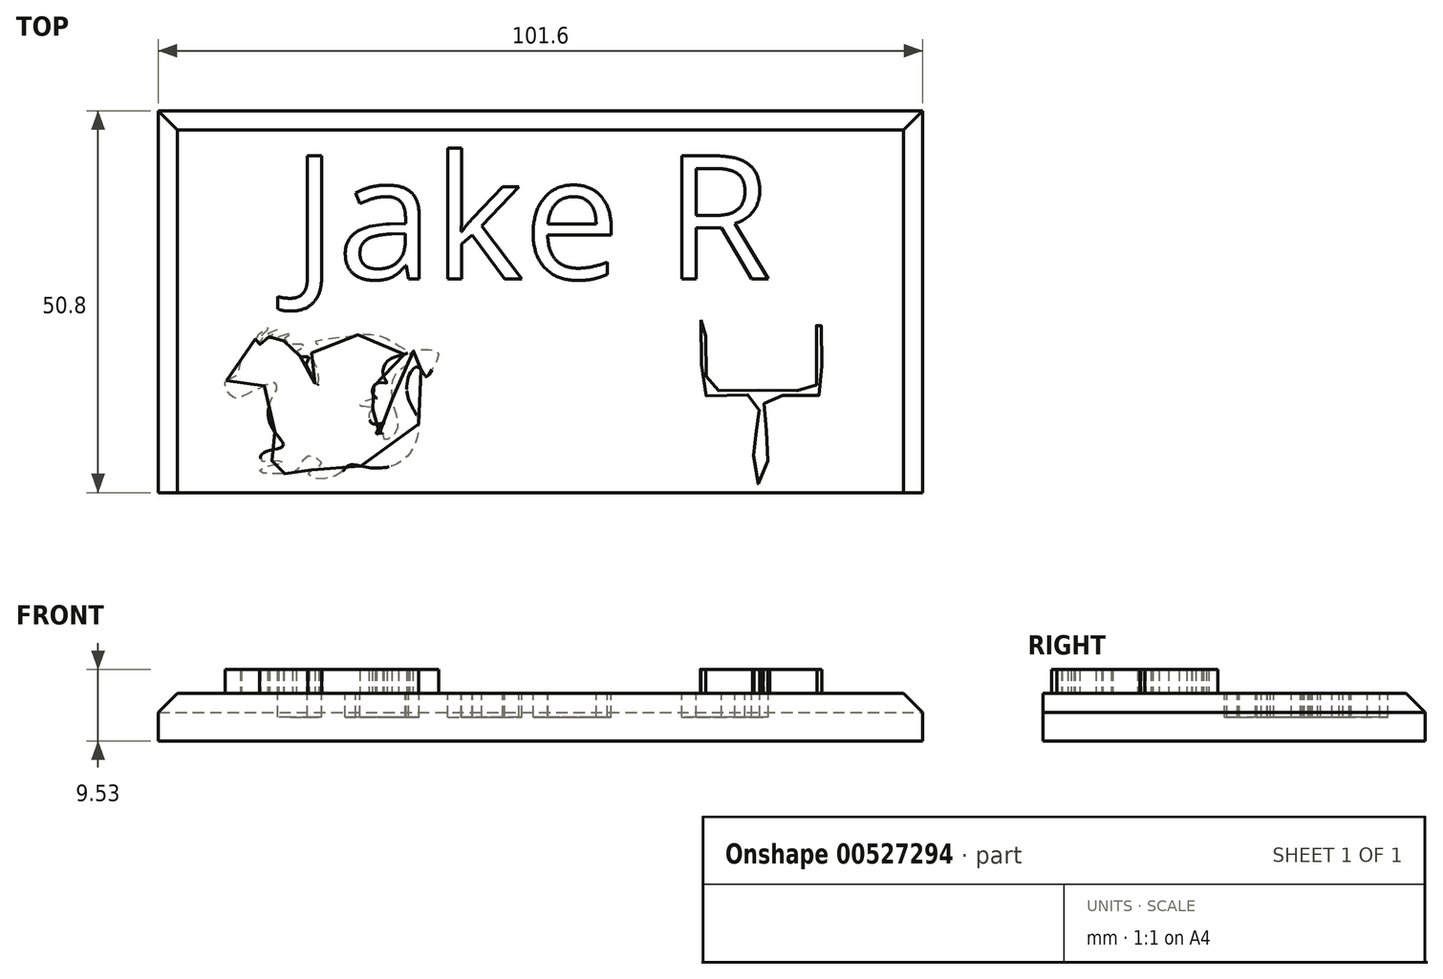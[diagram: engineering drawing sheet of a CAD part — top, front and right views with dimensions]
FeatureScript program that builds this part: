
annotation { "Feature Type Name" : "Feature", "Feature Type Description" : "" }
export const myFeature = defineFeature(function(context is Context, id is Id, definition is map)
    precondition{}
    {
        {
            var Q0;
            Q0=qCreatedBy(makeId("Top.planeOp"),FACE);
            var sketch = newSketch(context, id + "F0", { "sketchPlane" : qUnion([Q0])});
            skLineSegment(sketch, "E0.bottom", {"start": v(-19.05, 19.06) * mm, "end": v(82.55, 19.06) * mm});
            skLineSegment(sketch, "E0.top", {"start": v(-19.05, -31.74) * mm, "end": v(82.55, -31.74) * mm});
            skLineSegment(sketch, "E0.left", {"start": v(-19.05, 19.06) * mm, "end": v(-19.05, -31.74) * mm});
            skLineSegment(sketch, "E0.right", {"start": v(82.55, 19.06) * mm, "end": v(82.55, -31.74) * mm});
            skSolve(sketch);
        }
        {
            var Q0;
            Q0 = qSketchRegion(id + "F0", true);
            extrude(context, id + "F1", {"entities" : qUnion([Q0]), "depth" : 6.35 * mm, "offsetDistance" : 25.4 * mm});
        }
        {
            var Q0;
            Q0=makeQuery(id+"F1.opExtrude","CAP_FACE",FACE,{"disambiguationData":[OSD([sQuery(id+"F0.wireOp",EDGE,"E0.bottom"),sQuery(id+"F0.wireOp",EDGE,"E0.top"),sQuery(id+"F0.wireOp",EDGE,"E0.left"),sQuery(id+"F0.wireOp",EDGE,"E0.right")])],"isStart":false});
            var sketch = newSketch(context, id + "F2", { "sketchPlane" : qUnion([Q0])});
            skPoint(sketch, "E1.firstSnap0", {"position": v(-19.05, -6.34) * mm});
            skText(sketch, "E2", { "text": "Jake R", "fontName": "OpenSans-Regular.ttf"});
            const initialGuessF2  = {"E2": [-0.00136, -0.00328, 1, 0, 0.01648]};
            skSetInitialGuess(sketch, initialGuessF2);
            skSolve(sketch);
        }
        {
            var Q0;
            Q0 = qSketchRegion(id + "F2", true);
            extrude(context, id + "F3", {"entities" : qUnion([Q0]), "operationType" : NewBodyOperationType.REMOVE, "oppositeDirection" : true, "depth" : 3.17 * mm, "offsetDistance" : 25.4 * mm});
        }
        {
            var Q0;
            {var subQ0=sQuery(id+"F0.wireOp",EDGE,"E0.left");var subQ1=sQuery(id+"F0.wireOp",EDGE,"E0.bottom");var subQ2=sQuery(id+"F0.wireOp",EDGE,"E0.right");var subQ3=sQuery(id+"F0.wireOp",EDGE,"E0.top");Q0=makeQuery(id+"F3.boolean.opBoolean","SPLIT",FACE,{"disambiguationData":[TD([makeQuery(id+"F1.opExtrude","SWEPT_FACE",FACE,{"disambiguationData":[OSD([subQ1])]})])],"derivedFrom":makeQuery(id+"F1.opExtrude","CAP_FACE",FACE,{"disambiguationData":[OSD([subQ1,subQ3,subQ0,subQ2])],"isStart":false})});}
            var sketch = newSketch(context, id + "F4", { "sketchPlane" : qUnion([Q0])});
            skSolve(sketch);
        }
        {
            var Q0;
            Q0=makeQuery(id+"F4.imprint","IMPRINT",FACE,{"disambiguationData":[TD([[makeQuery(id+"F4.imprint","IMPRINT",EDGE,{"derivedFrom":makeQuery(id+"F1.opExtrude","CAP_EDGE",EDGE,{"disambiguationData":[OSD([sQuery(id+"F0.wireOp",EDGE,"E0.bottom")])],"isStart":false})}),-1.0]])]});
            var sketch = newSketch(context, id + "F5", { "sketchPlane" : qUnion([Q0])});
            skFitSpline(sketch, "E3", {"points": [v(-9.95, -16.83) * mm, v(-8.47, -16.02) * mm, v(-8.07, -14.08) * mm, v(-8.14, -13.88) * mm, v(-6.53, -12.13) * mm, v(-6.4, -11.8) * mm, v(-5.19, -10.14) * mm, v(-4.48, -9.74) * mm, v(-4.29, -9.74) * mm, v(-4.38, -9.9) * mm, v(-5.19, -10.52) * mm, v(-5.69, -11.52) * mm, v(-5.66, -12) * mm, v(-5.45, -11.97) * mm, v(-5.33, -11.35) * mm, v(-4.43, -10.52) * mm, v(-3.74, -10.21) * mm, v(-3.13, -10.02) * mm, v(-3.03, -10.07) * mm, v(-3.54, -10.41) * mm, v(-4.4, -11.08) * mm, v(-4.48, -11.4) * mm, v(-3.08, -10.97) * mm, v(-1.64, -10.5) * mm, v(-1.24, -10.4) * mm, v(-1.38, -10.61) * mm, v(-2.28, -11.2) * mm, v(-2.26, -11.82) * mm, v(-1.16, -11.97) * mm, v(0.54, -12.04) * mm, v(0.61, -12.2) * mm, v(-0.26, -12.46) * mm, v(-0.67, -13.24) * mm, v(0, -13.64) * mm, v(0.92, -13.72) * mm, v(0.8, -14.15) * mm, v(0.64, -14.8) * mm, v(0.92, -15.31) * mm, v(1.2, -16.03) * mm, v(1.48, -16.79) * mm, v(1.88, -17.26) * mm, v(2.16, -17.38) * mm, v(2.28, -16.27) * mm, v(2.04, -15.2) * mm, v(1.6, -14.23) * mm, v(1.24, -13.64) * mm, v(1.04, -13.4) * mm, v(1.56, -13.04) * mm, v(2.28, -12.68) * mm, v(2.8, -12.4) * mm, v(1.76, -11.76) * mm, v(6.1, -10.93) * mm, v(9.38, -10.66) * mm, v(11.52, -11.33) * mm, v(13.4, -12.47) * mm, v(14.14, -13.08) * mm, v(13, -13.48) * mm, v(11.19, -14.49) * mm, v(10.92, -16.36) * mm, v(11.32, -17.1) * mm, v(9.91, -17.24) * mm, v(9.51, -18.71) * mm, v(9.98, -19.18) * mm, v(9.27, -19.31) * mm, v(7.77, -20.09) * mm, v(9.74, -20.4) * mm, v(9.17, -20.92) * mm, v(9.02, -21.95) * mm, v(9.58, -22.62) * mm, v(10.93, -22.47) * mm, v(10.36, -23.04) * mm, v(10, -23.92) * mm, v(10.72, -23.81) * mm, v(10.98, -24.64) * mm, v(12.58, -23.66) * mm, v(12.8, -22) * mm, v(12.12, -19.52) * mm, v(12.43, -16) * mm, v(14.19, -14.6) * mm, v(14.78, -13.74) * mm, v(14.37, -13.27) * mm, v(15.38, -12.73) * mm, v(18, -12.93) * mm, v(18.13, -13.74) * mm, v(16.59, -16.29) * mm, v(16.18, -15.82) * mm, v(15.25, -15.01) * mm, v(14.1, -16.76) * mm, v(14.37, -19.7) * mm, v(15.51, -22.12) * mm, v(14.66, -26.05) * mm, v(11.96, -28.2) * mm, v(8.35, -28.3) * mm, v(6.32, -28.08) * mm, v(5.08, -29.2) * mm, v(1.47, -29.77) * mm, v(0.9, -28.98) * mm, v(2.6, -28.08) * mm, v(2.48, -27.51) * mm, v(0.68, -26.95) * mm, v(-0.68, -28.87) * mm, v(-2.93, -29.2) * mm, v(-5.53, -28.98) * mm, v(-4.96, -28.3) * mm, v(-2.37, -27.74) * mm, v(-4.17, -27.51) * mm, v(-5.3, -27.51) * mm, v(-5.3, -26.61) * mm, v(-2.7, -25.7) * mm, v(-2.48, -25.15) * mm, v(-4.06, -22.78) * mm, v(-4.17, -19.62) * mm, v(-3.27, -17.81) * mm, v(-3.6, -17.14) * mm, v(-4.85, -17.48) * mm, v(-7.22, -18.6) * mm, v(-8.68, -19.17) * mm, v(-9.7, -18.5) * mm, v(-10.15, -17.36) * mm, v(-9.95, -16.83) * mm]});
            skSolve(sketch);
        }
        {
            var Q0;
            Q0 = qSketchRegion(id + "F5", true);
            extrude(context, id + "F6", {"entities" : qUnion([Q0]), "operationType" : NewBodyOperationType.ADD, "depth" : 3.17 * mm, "offsetDistance" : 25.4 * mm});
        }
        {
            var Q0;
            Q0=makeQuery(id+"F4.imprint","IMPRINT",FACE,{"disambiguationData":[TD([[makeQuery(id+"F4.imprint","IMPRINT",EDGE,{"derivedFrom":makeQuery(id+"F1.opExtrude","CAP_EDGE",EDGE,{"disambiguationData":[OSD([sQuery(id+"F0.wireOp",EDGE,"E0.bottom")])],"isStart":false})}),-1.0]])]});
            var sketch = newSketch(context, id + "F7", { "sketchPlane" : qUnion([Q0])});
            skFitSpline(sketch, "E4", {"points": [v(53.08, -8.8) * mm, v(53.11, -11.61) * mm, v(53.15, -15.6) * mm, v(53.15, -18.58) * mm, v(53.44, -18.88) * mm, v(55.17, -18.74) * mm, v(58.29, -18.78) * mm, v(61, -18.71) * mm, v(60.94, -18.94) * mm, v(60.84, -20.4) * mm, v(60.88, -21.42) * mm, v(60.88, -22.84) * mm, v(60.84, -23.47) * mm, v(60.33, -23.55) * mm, v(60.1, -23.9) * mm, v(59.93, -25.24) * mm, v(60.1, -26.95) * mm, v(60.1, -29.24) * mm, v(60.31, -30.4) * mm, v(61.04, -30.58) * mm, v(61.93, -30.4) * mm, v(61.99, -28.4) * mm, v(62.16, -25.5) * mm, v(62.21, -24.16) * mm, v(61.76, -23.5) * mm, v(61.43, -23.38) * mm, v(61.43, -21.98) * mm, v(61.43, -19.7) * mm, v(61.49, -18.97) * mm, v(62.27, -18.86) * mm, v(63.83, -18.8) * mm, v(67.29, -18.8) * mm, v(68.46, -18.8) * mm, v(69.07, -18.75) * mm, v(69.13, -17.8) * mm, v(69.13, -15.07) * mm, v(69.13, -12.28) * mm, v(69.08, -9.47) * mm, v(69.08, -8.74) * mm, v(68.88, -8.58) * mm, v(68.6, -8.55) * mm, v(68.45, -9) * mm, v(68.45, -9.7) * mm, v(68.43, -10.7) * mm, v(68.46, -12.23) * mm, v(68.43, -13.62) * mm, v(68.44, -15.21) * mm, v(68.42, -17.42) * mm, v(68.44, -18.2) * mm, v(68.02, -18.17) * mm, v(66.59, -18.15) * mm, v(63.77, -18.12) * mm, v(61.47, -18.08) * mm, v(59.43, -18.1) * mm, v(56.2, -18.15) * mm, v(54.16, -18.12) * mm, v(53.73, -18.1) * mm, v(53.7, -17.65) * mm, v(53.76, -15.12) * mm, v(53.7, -12.99) * mm, v(53.73, -9.6) * mm, v(53.73, -8.78) * mm, v(53.51, -8.61) * mm, v(53.26, -8.6) * mm, v(53.08, -8.8) * mm]});
            skSolve(sketch);
        }
        {
            var Q0;
            Q0 = qSketchRegion(id + "F7", true);
            extrude(context, id + "F8", {"entities" : qUnion([Q0]), "operationType" : NewBodyOperationType.ADD, "depth" : 3.17 * mm, "offsetDistance" : 25.4 * mm});
        }
        {
            var Q0;
            Q0=makeQuery(id+"F1.opExtrude","CAP_EDGE",EDGE,{"disambiguationData":[OSD([sQuery(id+"F0.wireOp",EDGE,"E0.left")])],"isStart":false});
            var Q1;
            Q1=makeQuery(id+"F1.opExtrude","CAP_EDGE",EDGE,{"disambiguationData":[OSD([sQuery(id+"F0.wireOp",EDGE,"E0.bottom")])],"isStart":false});
            var Q2;
            Q2=makeQuery(id+"F1.opExtrude","CAP_EDGE",EDGE,{"disambiguationData":[OSD([sQuery(id+"F0.wireOp",EDGE,"E0.right")])],"isStart":false});
            chamfer(context, id + "F9", {"entities" : qUnion([Q0, Q1, Q2]), "width" : 2.54 * mm, "tangentPropagation" : true});
        }
    });
